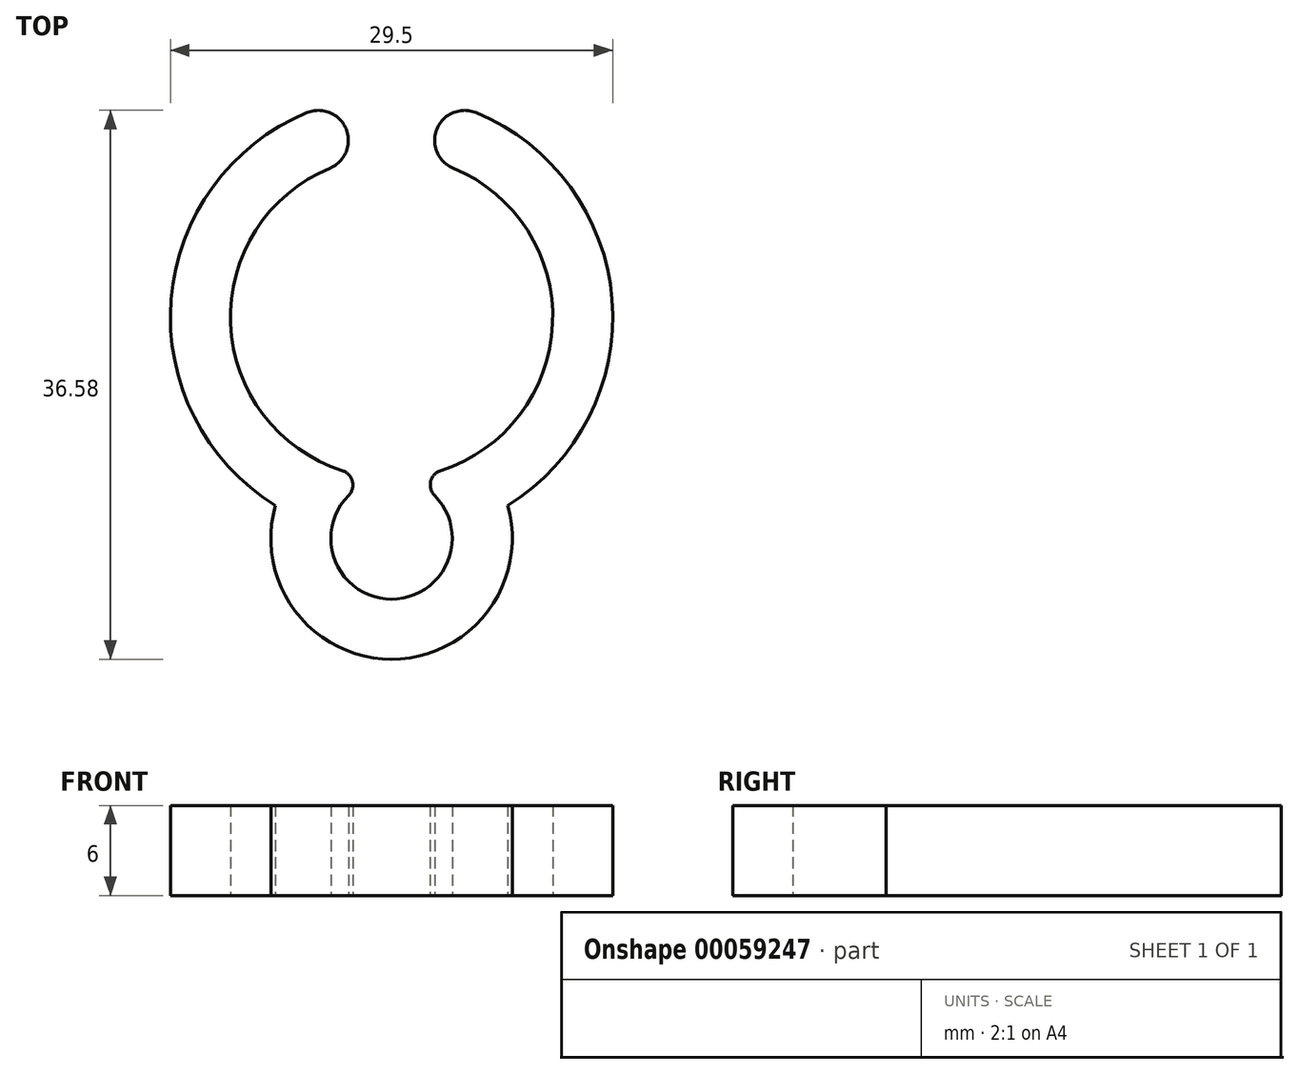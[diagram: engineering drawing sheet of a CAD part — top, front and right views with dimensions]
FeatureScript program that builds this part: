
annotation { "Feature Type Name" : "Feature", "Feature Type Description" : "" }
export const myFeature = defineFeature(function(context is Context, id is Id, definition is map)
    precondition{}
    {
        {
            var Q0;
            Q0=qCreatedBy(makeId("Top.planeOp"),FACE);
            var sketch = newSketch(context, id + "F0", { "sketchPlane" : qUnion([Q0])});
            skArc(sketch, "E0", {"start": v(-4.11, 9.93) * mm, "mid": v(0, 10.75) * mm, "end": v(4.11, 9.93) * mm, "construction": true});
            skLineSegment(sketch, "E1", {"start": v(-4.11, 9.93) * mm, "end": v(0, 0) * mm, "construction": true});
            skLineSegment(sketch, "E2", {"start": v(0, 10.75) * mm, "end": v(0, 0) * mm, "construction": true});
            skLineSegment(sketch, "E3", {"start": v(0, 0) * mm, "end": v(4.11, 9.93) * mm, "construction": true});
            skArc(sketch, "E4", {"start": v(-4.11, 9.93) * mm, "mid": v(-10.74, -0.45) * mm, "end": v(-3.28, -10.24) * mm});
            skArc(sketch, "E5.0", {"start": v(-5.64, 13.63) * mm, "mid": v(-14.7, 1.18) * mm, "end": v(-7.74, -12.55) * mm});
            skLineSegment(sketch, "E6", {"start": v(-5.64, 13.63) * mm, "end": v(-4.11, 9.93) * mm, "construction": true});
            skLineSegment(sketch, "E7", {"start": v(5.64, 13.63) * mm, "end": v(4.11, 9.93) * mm, "construction": true});
            skArc(sketch, "E8", {"start": v(-4.11, 9.93) * mm, "mid": v(-3.03, 12.54) * mm, "end": v(-5.64, 13.63) * mm});
            skArc(sketch, "E9", {"start": v(5.64, 13.63) * mm, "mid": v(3.03, 12.54) * mm, "end": v(4.11, 9.93) * mm});
            skArc(sketch, "E10", {"start": v(-2.87, -11.9) * mm, "mid": v(0, -18.8) * mm, "end": v(2.87, -11.9) * mm});
            skArc(sketch, "E11.0", {"start": v(-7.74, -12.55) * mm, "mid": v(0, -22.8) * mm, "end": v(7.74, -12.55) * mm});
            skArc(sketch, "E12.trimOffspring", {"start": v(7.74, -12.55) * mm, "mid": v(14.7, 1.18) * mm, "end": v(5.64, 13.63) * mm});
            skArc(sketch, "E13.trimOffspring", {"start": v(3.28, -10.24) * mm, "mid": v(10.74, -0.45) * mm, "end": v(4.11, 9.93) * mm});
            skPoint(sketch, "E14.visualSharp", {"position": v(-0.54, -10.74) * mm});
            skArc(sketch, "E14.filletArc", {"start": v(-2.87, -11.9) * mm, "mid": v(-2.61, -10.95) * mm, "end": v(-3.28, -10.24) * mm});
            skPoint(sketch, "E15.visualSharp", {"position": v(0.54, -10.74) * mm});
            skArc(sketch, "E15.filletArc", {"start": v(3.28, -10.24) * mm, "mid": v(2.61, -10.95) * mm, "end": v(2.87, -11.9) * mm});
            skSolve(sketch);
        }
        {
            var Q0;
            Q0=makeQuery(id+"F0.imprint","IMPRINT",FACE,{"disambiguationData":[TD([[makeQuery(id+"F0.imprint","IMPRINT",EDGE,{"derivedFrom":sQuery(id+"F0.wireOp",EDGE,"E4")}),-1.0]])]});
            extrude(context, id + "F1", {"entities" : qUnion([Q0]), "depth" : 6 * mm});
        }
    });
